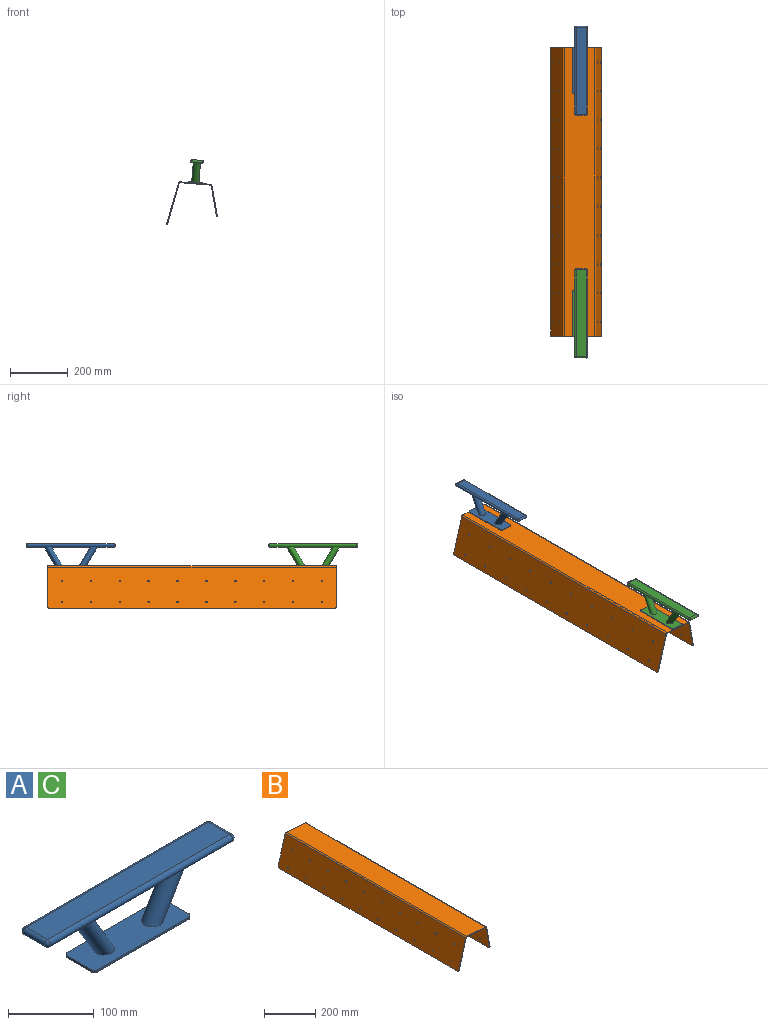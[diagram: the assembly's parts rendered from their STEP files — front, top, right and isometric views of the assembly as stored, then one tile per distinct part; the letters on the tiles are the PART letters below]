
ASSEMBLY  parts=3 mates=2
PART A: 22 faces, bbox 310x50x80 mm
  f0: plane 150x3mm, normal (0,1,0), area 450mm2, adj f3,f4,f13,f20
  f1: plane 40x3mm, normal (-1,0,0), area 120mm2, adj f3,f4,f13,f14
  f2: plane 150x3mm, normal (0,-1,0), area 450mm2, adj f3,f4,f14,f21
  f3: plane 160x50mm, normal (0,0,1), area 6996.8mm2, adj f0,f1,f2,f5,f13,f14,f15,f16
  f4: plane 160x50mm, normal (0,0,-1), area 7978.5mm2, adj f0,f1,f2,f13,f14,f15,f20,f21
  f5: bspline ~67x65mm, area 5715.5mm2, adj f3,f7
  f6: cylinder r=5mm len=300mm, axis (1,0,0), area 4712.4mm2, adj f7,f9,f11,f18
  f7: plane 300x35mm, normal (0,0,-1), area 9518.3mm2, adj f5,f6,f8,f10,f16,f17
  f8: cylinder r=5mm len=300mm, axis (1,0,0), area 4712.4mm2, adj f7,f9,f12,f19
  f9: plane 300x35mm, normal (0,0,1), area 10500mm2, adj f6,f8,f10,f17
  f10: cylinder r=5mm len=35mm, axis (0,1,0), area 549.8mm2, adj f7,f9,f11,f12
  f11: sphere r=5mm, area 78.5mm2, adj f6,f10
  f12: sphere r=5mm, area 78.5mm2, adj f8,f10
  f13: cylinder r=5mm len=5mm, axis (0,0,1), area 23.6mm2, adj f0,f1,f3,f4
  f14: cylinder r=5mm len=5mm, axis (0,0,-1), area 23.6mm2, adj f1,f2,f3,f4
  f15: plane 40x3mm, normal (1,0,0), area 120mm2, adj f3,f4,f20,f21
  f16: bspline ~67x65mm, area 5715.5mm2, adj f3,f7
  f17: cylinder r=5mm len=35mm, axis (0,1,0), area 549.8mm2, adj f7,f9,f18,f19
  f18: sphere r=5mm, area 78.5mm2, adj f6,f17
  f19: sphere r=5mm, area 78.5mm2, adj f8,f17
  f20: cylinder r=5mm len=5mm, axis (0,0,1), area 23.6mm2, adj f0,f3,f4,f15
  f21: cylinder r=5mm len=5mm, axis (0,0,-1), area 23.6mm2, adj f2,f3,f4,f15
PART B: 66 faces, bbox 175.9x1000x147 mm
  f0: plane 102.02x20.85mm, normal (0,1,0), area 309.2mm2, adj f23,f24,f26,f63
  f1: plane 102.02x20.85mm, normal (0,-1,0), area 309.2mm2, adj f23,f24,f25,f62
  f2: cylinder r=3mm len=6.43mm, axis (0.98,0,0.17), area 56.5mm2, adj f23,f24
  f3: cylinder r=3mm len=6.43mm, axis (0.98,0,0.17), area 56.5mm2, adj f23,f24
  f4: cylinder r=3mm len=6.43mm, axis (0.98,0,0.17), area 56.5mm2, adj f23,f24
  f5: cylinder r=3mm len=6.43mm, axis (0.98,0,0.17), area 56.5mm2, adj f23,f24
  f6: cylinder r=3mm len=6.43mm, axis (0.98,0,0.17), area 56.5mm2, adj f23,f24
  f7: cylinder r=3mm len=6.43mm, axis (0.98,0,0.17), area 56.5mm2, adj f23,f24
  f8: cylinder r=3mm len=6.43mm, axis (0.98,0,0.17), area 56.5mm2, adj f23,f24
  f9: cylinder r=3mm len=6.43mm, axis (0.98,0,0.17), area 56.5mm2, adj f23,f24
  f10: cylinder r=3mm len=6.43mm, axis (0.98,0,0.17), area 56.5mm2, adj f23,f24
  f11: cylinder r=3mm len=6.43mm, axis (0.98,0,0.17), area 56.5mm2, adj f23,f24
  f12: cylinder r=3mm len=6.43mm, axis (0.98,0,0.17), area 56.5mm2, adj f23,f24
  f13: cylinder r=3mm len=6.43mm, axis (0.98,0,0.17), area 56.5mm2, adj f23,f24
  f14: cylinder r=3mm len=6.43mm, axis (0.98,0,0.17), area 56.5mm2, adj f23,f24
  f15: cylinder r=3mm len=6.43mm, axis (0.98,0,0.17), area 56.5mm2, adj f23,f24
  f16: cylinder r=3mm len=6.43mm, axis (0.98,0,0.17), area 56.5mm2, adj f23,f24
  f17: cylinder r=3mm len=6.43mm, axis (0.98,0,0.17), area 56.5mm2, adj f23,f24
  f18: cylinder r=3mm len=6.43mm, axis (0.98,0,0.17), area 56.5mm2, adj f23,f24
  f19: cylinder r=3mm len=6.43mm, axis (0.98,0,0.17), area 56.5mm2, adj f23,f24
  f20: cylinder r=3mm len=6.43mm, axis (0.98,0,0.17), area 56.5mm2, adj f23,f24
  f21: cylinder r=3mm len=6.43mm, axis (0.98,0,0.17), area 56.5mm2, adj f23,f24
  f22: plane 990x2.95mm, normal (0.17,0,-0.98), area 2970mm2, adj f23,f24,f25,f26
  f23: plane 1000x106.42mm, normal (0.98,0,0.17), area 107488.1mm2, adj f0,f1,f2,f3,f4,f5,f6,f7
  f24: plane 1000x106.42mm, normal (-0.98,0,-0.17), area 107488.1mm2, adj f0,f1,f2,f3,f4,f5,f6,f7
  f25: cylinder r=5mm len=5.45mm, axis (0.98,0,0.17), area 23.6mm2, adj f1,f22,f23,f24
  f26: cylinder r=5mm len=5.45mm, axis (-0.98,0,-0.17), area 23.6mm2, adj f0,f22,f23,f24
  f27: plane 105.93x11.31mm, normal (0,1,0), area 318.1mm2, adj f29,f30,f59,f63
  f28: plane 105.93x11.31mm, normal (0,-1,0), area 318.1mm2, adj f29,f30,f58,f62
  f29: plane 1000x105.7mm, normal (0.08,0,1), area 106021.7mm2, adj f27,f28,f60,f64
  f30: plane 1000x105.7mm, normal (-0.08,0,-1), area 106021.7mm2, adj f27,f28,f61,f65
  f31: plane 138.25x42.29mm, normal (0,1,0), area 428.9mm2, adj f54,f55,f56,f59
  f32: plane 990x2.88mm, normal (-0.28,0,-0.96), area 2970mm2, adj f54,f55,f56,f57
  f33: plane 138.25x42.29mm, normal (0,-1,0), area 428.9mm2, adj f54,f55,f57,f58
  f34: cylinder r=2.5mm len=5.63mm, axis (-0.96,0,0.28), area 47.1mm2, adj f54,f55
  f35: cylinder r=2.5mm len=5.63mm, axis (-0.96,0,0.28), area 47.1mm2, adj f54,f55
  f36: cylinder r=2.5mm len=5.63mm, axis (-0.96,0,0.28), area 47.1mm2, adj f54,f55
  f37: cylinder r=2.5mm len=5.63mm, axis (-0.96,0,0.28), area 47.1mm2, adj f54,f55
  f38: cylinder r=2.5mm len=5.63mm, axis (-0.96,0,0.28), area 47.1mm2, adj f54,f55
  f39: cylinder r=2.5mm len=5.63mm, axis (-0.96,0,0.28), area 47.1mm2, adj f54,f55
  f40: cylinder r=2.5mm len=5.63mm, axis (-0.96,0,0.28), area 47.1mm2, adj f54,f55
  f41: cylinder r=2.5mm len=5.63mm, axis (-0.96,0,0.28), area 47.1mm2, adj f54,f55
  f42: cylinder r=2.5mm len=5.63mm, axis (-0.96,0,0.28), area 47.1mm2, adj f54,f55
  f43: cylinder r=2.5mm len=5.63mm, axis (-0.96,0,0.28), area 47.1mm2, adj f54,f55
  f44: cylinder r=2.5mm len=5.63mm, axis (-0.96,0,0.28), area 47.1mm2, adj f54,f55
  f45: cylinder r=2.5mm len=5.63mm, axis (-0.96,0,0.28), area 47.1mm2, adj f54,f55
  f46: cylinder r=2.5mm len=5.63mm, axis (-0.96,0,0.28), area 47.1mm2, adj f54,f55
  f47: cylinder r=2.5mm len=5.63mm, axis (-0.96,0,0.28), area 47.1mm2, adj f54,f55
  f48: cylinder r=2.5mm len=5.63mm, axis (-0.96,0,0.28), area 47.1mm2, adj f54,f55
  f49: cylinder r=2.5mm len=5.63mm, axis (-0.96,0,0.28), area 47.1mm2, adj f54,f55
  f50: cylinder r=2.5mm len=5.63mm, axis (-0.96,0,0.28), area 47.1mm2, adj f54,f55
  f51: cylinder r=2.5mm len=5.63mm, axis (-0.96,0,0.28), area 47.1mm2, adj f54,f55
  f52: cylinder r=2.5mm len=5.63mm, axis (-0.96,0,0.28), area 47.1mm2, adj f54,f55
  f53: cylinder r=2.5mm len=5.63mm, axis (-0.96,0,0.28), area 47.1mm2, adj f54,f55
  f54: plane 1000x142.23mm, normal (-0.96,0,0.28), area 147554mm2, adj f31,f32,f33,f34,f35,f36,f37,f38
  f55: plane 1000x142.23mm, normal (0.96,0,-0.28), area 147554mm2, adj f31,f32,f33,f34,f35,f36,f37,f38
  f56: cylinder r=5mm len=5.63mm, axis (-0.96,0,0.28), area 23.6mm2, adj f31,f32,f54,f55
  f57: cylinder r=5mm len=5.63mm, axis (0.96,0,-0.28), area 23.6mm2, adj f32,f33,f54,f55
  f58: plane 5.72x4.81mm, normal (0,-1,0), area 16.4mm2, adj f28,f33,f60,f61
  f59: plane 5.72x4.81mm, normal (0,1,0), area 16.4mm2, adj f27,f31,f60,f61
  f60: cylinder r=5.5mm len=1000mm, axis (0,-1,0), area 7535.5mm2, adj f29,f54,f58,f59
  f61: cylinder r=2.5mm len=1000mm, axis (0,-1,0), area 3425.2mm2, adj f30,f55,f58,f59
  f62: plane 5.22x5.05mm, normal (0,-1,0), area 15.8mm2, adj f1,f28,f64,f65
  f63: plane 5.22x5.05mm, normal (0,1,0), area 15.8mm2, adj f0,f27,f64,f65
  f64: cylinder r=5.5mm len=1000mm, axis (0,-1,0), area 7247.5mm2, adj f23,f29,f62,f63
  f65: cylinder r=2.5mm len=1000mm, axis (0,-1,0), area 3294.3mm2, adj f24,f30,f62,f63
PART C: same geometry as A
PLACE A rot(axis=(0.04,0.04,1),90.1deg) t=(-189.22,223.83,-51.2)mm
PLACE B t=(-188.64,303.83,-167.13)mm
PLACE C rot(axis=(0.04,0.04,1),90.1deg) t=(-189.22,-616.17,-51.2)mm
MATE fastened C.f4 <-> B.f29  axis (-0.08,0,-1) through (-189.22,-616.17,-51.2)mm
MATE fastened A.f4 <-> B.f29  axis (-0.08,0,-1) through (-189.22,223.83,-51.2)mm
